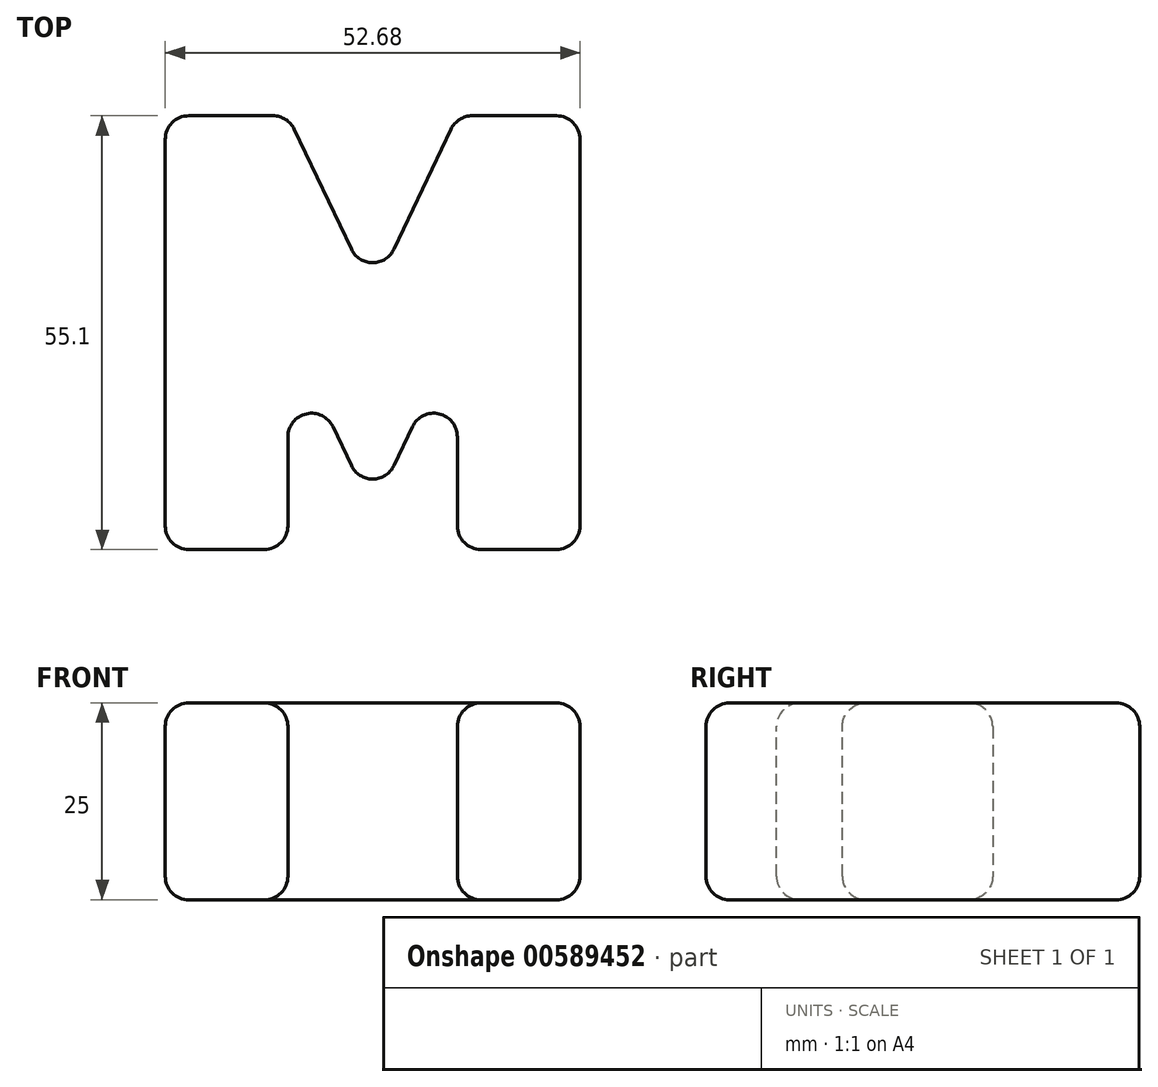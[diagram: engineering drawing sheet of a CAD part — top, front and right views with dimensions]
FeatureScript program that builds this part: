
annotation { "Feature Type Name" : "Feature", "Feature Type Description" : "" }
export const myFeature = defineFeature(function(context is Context, id is Id, definition is map)
    precondition{}
    {
        {
            var Q0;
            Q0=qCreatedBy(makeId("Top.planeOp"),FACE);
            var sketch = newSketch(context, id + "F0", { "sketchPlane" : qUnion([Q0])});
            skLineSegment(sketch, "E0", {"start": v(-26.34, 55.1) * mm, "end": v(-26.34, 0) * mm});
            skLineSegment(sketch, "E1", {"start": v(-26.34, 55.1) * mm, "end": v(-10.76, 55.1) * mm});
            skLineSegment(sketch, "E2", {"start": v(0, 55.1) * mm, "end": v(0, 0) * mm});
            skLineSegment(sketch, "E3", {"start": v(-26.34, 0) * mm, "end": v(-10.76, 0) * mm});
            skLineSegment(sketch, "E4.MirrorCS", {"start": v(-26.34, 110.2) * mm, "end": v(-10.76, 110.2) * mm});
            skLineSegment(sketch, "E5", {"start": v(-10.76, 55.1) * mm, "end": v(0, 32.43) * mm});
            skLineSegment(sketch, "E6", {"start": v(-10.76, 0) * mm, "end": v(-10.76, 27.62) * mm});
            skLineSegment(sketch, "E7", {"start": v(-10.76, 27.62) * mm, "end": v(0, 4.96) * mm});
            skLineSegment(sketch, "E8.MirrorCS", {"start": v(10.76, 55.1) * mm, "end": v(0, 32.43) * mm});
            skLineSegment(sketch, "E9.MirrorCS", {"start": v(10.76, 27.62) * mm, "end": v(0, 4.96) * mm});
            skLineSegment(sketch, "E10.MirrorCS", {"start": v(10.76, 0) * mm, "end": v(10.76, 27.62) * mm});
            skLineSegment(sketch, "E11.MirrorCS", {"start": v(26.34, 55.1) * mm, "end": v(26.34, 0) * mm});
            skLineSegment(sketch, "E12.MirrorCS", {"start": v(26.34, 55.1) * mm, "end": v(10.76, 55.1) * mm});
            skLineSegment(sketch, "E13.MirrorCS", {"start": v(26.34, 0) * mm, "end": v(10.76, 0) * mm});
            skSolve(sketch);
        }
        {
            var Q0;
            Q0 = qSketchRegion(id + "F0", true);
            extrude(context, id + "F1", {"entities" : qUnion([Q0]), "depth" : 25 * mm, "offsetDistance" : 25 * mm});
        }
        {
            var Q0;
            Q0=makeQuery(id+"F1.opExtrude","CAP_FACE",FACE,{"disambiguationData":[OSD([sQuery(id+"F0.wireOp",EDGE,"E1"),sQuery(id+"F0.wireOp",EDGE,"E3"),sQuery(id+"F0.wireOp",EDGE,"E0"),sQuery(id+"F0.wireOp",EDGE,"E5"),sQuery(id+"F0.wireOp",EDGE,"E6"),sQuery(id+"F0.wireOp",EDGE,"E7"),sQuery(id+"F0.wireOp",EDGE,"E8.MirrorCS"),sQuery(id+"F0.wireOp",EDGE,"E9.MirrorCS"),sQuery(id+"F0.wireOp",EDGE,"E10.MirrorCS"),sQuery(id+"F0.wireOp",EDGE,"E11.MirrorCS"),sQuery(id+"F0.wireOp",EDGE,"E12.MirrorCS"),sQuery(id+"F0.wireOp",EDGE,"E13.MirrorCS")])],"isStart":false});
            var Q1;
            Q1=makeQuery(id+"F1.opExtrude","SWEPT_FACE",FACE,{"disambiguationData":[OSD([sQuery(id+"F0.wireOp",EDGE,"E11.MirrorCS")])]});
            var Q2;
            Q2=makeQuery(id+"F1.opExtrude","SWEPT_EDGE",EDGE,{"disambiguationData":[OSD([sQuery(id+"F0.wireOp",EDGE,"E8.MirrorCS"),sQuery(id+"F0.wireOp",EDGE,"E12.MirrorCS")])]});
            var Q3;
            Q3=makeQuery(id+"F1.opExtrude","CAP_FACE",FACE,{"disambiguationData":[OSD([sQuery(id+"F0.wireOp",EDGE,"E1"),sQuery(id+"F0.wireOp",EDGE,"E3"),sQuery(id+"F0.wireOp",EDGE,"E0"),sQuery(id+"F0.wireOp",EDGE,"E5"),sQuery(id+"F0.wireOp",EDGE,"E6"),sQuery(id+"F0.wireOp",EDGE,"E7"),sQuery(id+"F0.wireOp",EDGE,"E8.MirrorCS"),sQuery(id+"F0.wireOp",EDGE,"E9.MirrorCS"),sQuery(id+"F0.wireOp",EDGE,"E10.MirrorCS"),sQuery(id+"F0.wireOp",EDGE,"E11.MirrorCS"),sQuery(id+"F0.wireOp",EDGE,"E12.MirrorCS"),sQuery(id+"F0.wireOp",EDGE,"E13.MirrorCS")])],"isStart":true});
            var Q4;
            Q4=makeQuery(id+"F1.opExtrude","SWEPT_FACE",FACE,{"disambiguationData":[OSD([sQuery(id+"F0.wireOp",EDGE,"E10.MirrorCS")])]});
            var Q5;
            Q5=makeQuery(id+"F1.opExtrude","SWEPT_FACE",FACE,{"disambiguationData":[OSD([sQuery(id+"F0.wireOp",EDGE,"E7")])]});
            var Q6;
            Q6=makeQuery(id+"F1.opExtrude","SWEPT_FACE",FACE,{"disambiguationData":[OSD([sQuery(id+"F0.wireOp",EDGE,"E3")])]});
            var Q7;
            Q7=makeQuery(id+"F1.opExtrude","SWEPT_FACE",FACE,{"disambiguationData":[OSD([sQuery(id+"F0.wireOp",EDGE,"E1")])]});
            var Q8;
            Q8=makeQuery(id+"F1.opExtrude","SWEPT_FACE",FACE,{"disambiguationData":[OSD([sQuery(id+"F0.wireOp",EDGE,"E5")])]});
            fillet(context, id + "F2", {"entities" : qUnion([Q0, Q1, Q2, Q3, Q4, Q5, Q6, Q7, Q8]), "radius" : 3 * mm, "tangentPropagation" : true, "allowEdgeOverflow" : false});
        }
    });
